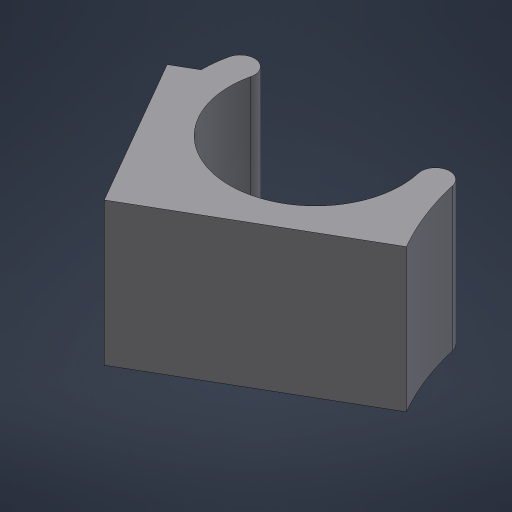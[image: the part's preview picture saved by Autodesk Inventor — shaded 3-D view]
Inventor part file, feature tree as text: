
AUTODESK INVENTOR PART (.ipt)
format: ipt  version: 2023.5 (Build 275446000, 446)  size: 372,736 bytes
history: native  units: mm
features: extrude x1, sketch x1
ambient origin geometry x8: Origin, YZ Plane, XZ Plane, XY Plane, X Axis, Y Axis, Z Axis, Center Point
bodies: Volumenkörper1 (feature_tree)
feature tree (2):
  extrude  "Extrusion1"  Depth=15.0mm
  sketch  "Skizze1"  dims[d0=18.0mm d1=3.0mm d2=2.0mm d4=18.0mm d5=13.0mm d6=120.0deg d7=15.0mm d8=0.0mm]
